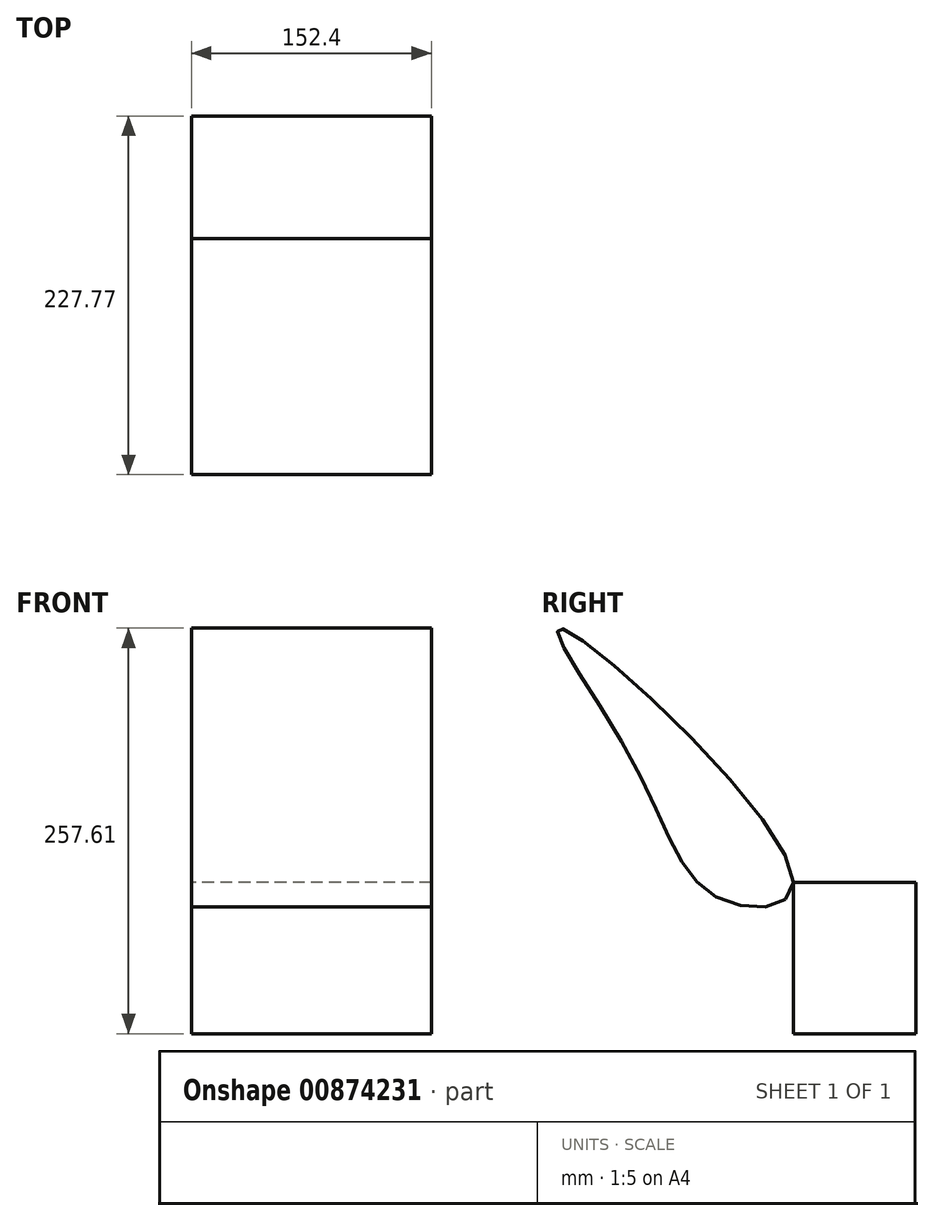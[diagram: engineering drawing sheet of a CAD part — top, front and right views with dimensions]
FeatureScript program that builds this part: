
annotation { "Feature Type Name" : "Feature", "Feature Type Description" : "" }
export const myFeature = defineFeature(function(context is Context, id is Id, definition is map)
    precondition{}
    {
        {
            var Q0;
            Q0=qCreatedBy(makeId("Right.planeOp"),FACE);
            var sketch = newSketch(context, id + "F0", { "sketchPlane" : qUnion([Q0])});
            skLineSegment(sketch, "E0.bottom", {"start": v(-41.98, 59.03) * mm, "end": v(35.85, 59.03) * mm});
            skLineSegment(sketch, "E0.top", {"start": v(-41.98, -37.03) * mm, "end": v(35.85, -37.03) * mm});
            skLineSegment(sketch, "E0.left", {"start": v(-41.98, 59.03) * mm, "end": v(-41.98, -37.03) * mm});
            skLineSegment(sketch, "E0.right", {"start": v(35.85, 59.03) * mm, "end": v(35.85, -37.03) * mm});
            skFitSpline(sketch, "E1", {"points": [v(-41.98, 59.03) * mm, v(-88.42, 48.61) * mm, v(-143.52, 134.95) * mm, v(-189.45, 220.47) * mm, v(-41.98, 59.03) * mm]});
            skSolve(sketch);
        }
        {
            var Q0;
            Q0=makeQuery(id+"F0.imprint","IMPRINT",FACE,{"disambiguationData":[TD([[makeQuery(id+"F0.imprint","IMPRINT",EDGE,{"derivedFrom":sQuery(id+"F0.wireOp",EDGE,"E1")}),-1.0]])]});
            var Q1;
            Q1=makeQuery(id+"F0.imprint","IMPRINT",FACE,{"disambiguationData":[TD([[makeQuery(id+"F0.imprint","IMPRINT",EDGE,{"derivedFrom":sQuery(id+"F0.wireOp",EDGE,"E0.bottom")}),-1.0]])]});
            extrude(context, id + "F1", {"entities" : qUnion([Q0, Q1]), "depth" : 152.4 * mm, "offsetDistance" : 25.4 * mm});
        }
    });
